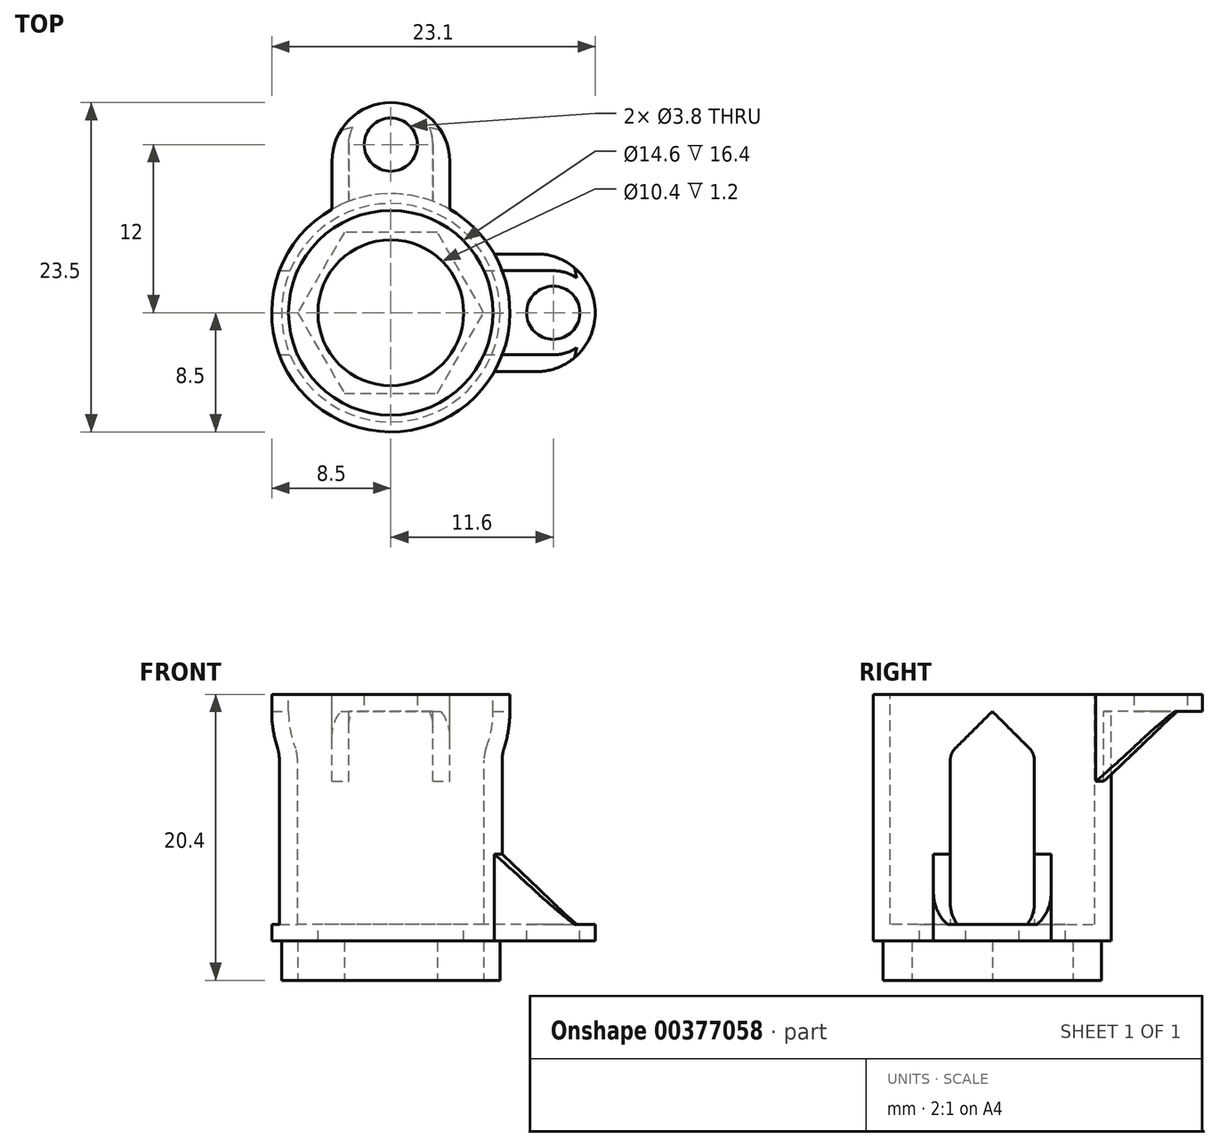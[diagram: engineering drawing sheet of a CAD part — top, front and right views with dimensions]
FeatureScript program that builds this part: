
annotation { "Feature Type Name" : "Feature", "Feature Type Description" : "" }
export const myFeature = defineFeature(function(context is Context, id is Id, definition is map)
    precondition{}
    {
        {
            var Q0;
            Q0=qCreatedBy(makeId("Front.planeOp"),FACE);
            var sketch = newSketch(context, id + "F0", { "sketchPlane" : qUnion([Q0])});
            skLineSegment(sketch, "E0", {"start": v(6.5, 0) * mm, "end": v(6.5, 26.4) * mm});
            skLineSegment(sketch, "E1", {"start": v(4.7, 0) * mm, "end": v(4.7, -6.4) * mm});
            skLineSegment(sketch, "E2", {"start": v(-3.7, 28.3) * mm, "end": v(3.7, 28.3) * mm});
            skPoint(sketch, "E3", {"position": v(0, 28.3) * mm});
            skLineSegment(sketch, "E4", {"start": v(-3.7, 40.8) * mm, "end": v(3.7, 40.8) * mm});
            skLineSegment(sketch, "E5", {"start": v(0, 26.4) * mm, "end": v(0, 0) * mm, "construction": true});
            skSolve(sketch);
        }
        {
            var Q0;
            Q0=qCreatedBy(makeId("Front.planeOp"),FACE);
            var sketch = newSketch(context, id + "F1", { "sketchPlane" : qUnion([Q0])});
            skLineSegment(sketch, "E6", {"start": v(7.3, 0) * mm, "end": v(7.3, 16.4) * mm});
            skLineSegment(sketch, "E7", {"start": v(7.3, 0) * mm, "end": v(5.2, 0) * mm});
            skLineSegment(sketch, "E8", {"start": v(5.2, 0) * mm, "end": v(5.2, -4) * mm});
            skLineSegment(sketch, "E9", {"start": v(5.2, -4) * mm, "end": v(7.8, -4) * mm});
            skLineSegment(sketch, "E10", {"start": v(7.8, -4) * mm, "end": v(7.8, -1.2) * mm});
            skLineSegment(sketch, "E11", {"start": v(8.5, -1.2) * mm, "end": v(8.5, 16.4) * mm});
            skLineSegment(sketch, "E12", {"start": v(7.3, 16.4) * mm, "end": v(8.5, 16.4) * mm});
            skPoint(sketch, "E13.orphan", {"position": v(0, -4) * mm});
            skLineSegment(sketch, "E14", {"start": v(8.5, -1.2) * mm, "end": v(7.8, -1.2) * mm});
            skSolve(sketch);
        }
        {
            var Q0;
            Q0 = qSketchRegion(id + "F1", true);
            var Q1;
            Q1=sQuery(id+"F0.wireOp",EDGE,"E5");
            revolve(context, id + "F2", {"entities" : qUnion([Q0]), "axis" : qUnion([Q1]), "revolveType" : RevolveType.FULL});
        }
        {
            var Q0;
            Q0=makeQuery(id+"F2.opRevolve","SWEPT_FACE",FACE,{"disambiguationData":[OSD([sQuery(id+"F1.wireOp",EDGE,"E9")])]});
            var sketch = newSketch(context, id + "F3", { "sketchPlane" : qUnion([Q0])});
            skCircle(sketch, "E15.cCircle", {"center": v(0, 0) * mm, "radius": 5.75 * mm, "construction": true});
            skLineSegment(sketch, "E15.0", {"start": v(-3.32, 5.75) * mm, "end": v(3.32, 5.75) * mm});
            skLineSegment(sketch, "E15.1", {"start": v(3.32, 5.75) * mm, "end": v(6.64, 0) * mm});
            skLineSegment(sketch, "E15.2", {"start": v(6.64, 0) * mm, "end": v(3.32, -5.75) * mm});
            skLineSegment(sketch, "E15.3", {"start": v(3.32, -5.75) * mm, "end": v(-3.32, -5.75) * mm});
            skLineSegment(sketch, "E15.4", {"start": v(-3.32, -5.75) * mm, "end": v(-6.64, 0) * mm});
            skLineSegment(sketch, "E15.5", {"start": v(-6.64, 0) * mm, "end": v(-3.32, 5.75) * mm});
            skPoint(sketch, "E15.0.midPoint", {"position": v(0, 5.75) * mm});
            skSolve(sketch);
        }
        {
            var Q0;
            Q0 = qSketchRegion(id + "F3", true);
            var Q1;
            Q1=qCreatedBy(makeId("Top.planeOp"),FACE);
            extrude(context, id + "F4", {"entities" : qUnion([Q0]), "operationType" : NewBodyOperationType.REMOVE, "oppositeDirection" : true, "endBoundEntityFace" : qUnion([Q1]), "depth" : (4 - 1.2) * mm});
        }
        {
            var Q0;
            Q0=makeQuery(id+"F2.opRevolve","SWEPT_FACE",FACE,{"disambiguationData":[OSD([sQuery(id+"F1.wireOp",EDGE,"E12")])]});
            var sketch = newSketch(context, id + "F5", { "sketchPlane" : qUnion([Q0])});
            skArc(sketch, "E16", {"start": v(4.2, 7.39) * mm, "mid": v(0, 8.5) * mm, "end": v(-4.2, 7.39) * mm});
            skArc(sketch, "E17", {"start": v(4.2, 10.8) * mm, "mid": v(0, 15) * mm, "end": v(-4.2, 10.8) * mm});
            skPoint(sketch, "E18", {"position": v(0, 15) * mm});
            skLineSegment(sketch, "E19", {"start": v(4.2, 10.8) * mm, "end": v(4.2, 7.39) * mm});
            skLineSegment(sketch, "E20", {"start": v(-4.2, 10.8) * mm, "end": v(-4.2, 7.39) * mm});
            skCircle(sketch, "E21", {"center": v(0, 12) * mm, "radius": 3 * mm, "construction": true});
            skPoint(sketch, "E22", {"position": v(-3, 12) * mm});
            skSolve(sketch);
        }
        {
            var Q0;
            Q0 = qSketchRegion(id + "F5", true);
            var Q1;
            Q1=qCreatedBy(makeId("Top.planeOp"),FACE);
            extrude(context, id + "F6", {"entities" : qUnion([Q0]), "operationType" : NewBodyOperationType.ADD, "endBound" : BoundingType.UP_TO_SURFACE, "oppositeDirection" : true, "endBoundEntityFace" : qUnion([Q1]), "depth" : 9 * mm});
        }
        {
            var Q0;
            Q0=qCreatedBy(makeId("Right.planeOp"),FACE);
            var sketch = newSketch(context, id + "F7", { "sketchPlane" : qUnion([Q0])});
            skLineSegment(sketch, "E23", {"start": v(15, 16.4) * mm, "end": v(15, 15.2) * mm, "construction": true});
            skLineSegment(sketch, "E24", {"start": v(13.5, 15.2) * mm, "end": v(8.5, 10.2) * mm});
            skLineSegment(sketch, "E25", {"start": v(8.5, 10.2) * mm, "end": v(8.5, 16.4) * mm, "construction": true});
            skLineSegment(sketch, "E26", {"start": v(8.5, 10.2) * mm, "end": v(8.5, 0) * mm});
            skLineSegment(sketch, "E27", {"start": v(8.5, 0) * mm, "end": v(15, 0) * mm});
            skLineSegment(sketch, "E28", {"start": v(15, 0) * mm, "end": v(15, 15.2) * mm});
            skLineSegment(sketch, "E29", {"start": v(13.5, 15.2) * mm, "end": v(15, 15.2) * mm});
            skSolve(sketch);
        }
        {
            var Q0;
            Q0 = qSketchRegion(id + "F7", true);
            var Q1;
            Q1=sQuery(id+"F0.wireOp",EDGE,"E5");
            revolve(context, id + "F8", {"operationType" : NewBodyOperationType.REMOVE, "entities" : qUnion([Q0]), "axis" : qUnion([Q1]), "revolveType" : RevolveType.FULL, "oppositeDirection" : true});
        }
        {
            var Q0;
            Q0=makeQuery(id+"F5.imprint","IMPRINT",FACE,{"disambiguationData":[TD([[makeQuery(id+"F5.imprint","IMPRINT",EDGE,{"derivedFrom":sQuery(id+"F5.wireOp",EDGE,"E16")}),-1.0]])]});
            cPlane(context, id + "F9", {"entities" : qUnion([Q0]), "cplaneType" : CPlaneType.OFFSET, "offset" : 1.2 * mm, "oppositeDirection" : true, "width" : 150 * mm, "height" : 150 * mm});
        }
        {
            var Q0;
            Q0=qCreatedBy(id+"F9.planeOp",FACE);
            var sketch = newSketch(context, id + "F10", { "sketchPlane" : qUnion([Q0])});
            skArc(sketch, "E30", {"start": v(3, 12) * mm, "mid": v(0, 15) * mm, "end": v(-3, 12) * mm});
            skArc(sketch, "E31", {"start": v(3, 7.95) * mm, "mid": v(0, 8.5) * mm, "end": v(-3, 7.95) * mm});
            skLineSegment(sketch, "E32", {"start": v(-3, 12) * mm, "end": v(-3, 7.95) * mm});
            skLineSegment(sketch, "E33", {"start": v(3, 12) * mm, "end": v(3, 7.95) * mm});
            skPoint(sketch, "E34", {"position": v(0, 15) * mm});
            skSolve(sketch);
        }
        {
            var Q0;
            Q0 = qSketchRegion(id + "F10", true);
            extrude(context, id + "F11", {"entities" : qUnion([Q0]), "operationType" : NewBodyOperationType.REMOVE, "endBound" : BoundingType.UP_TO_NEXT, "oppositeDirection" : true, "depth" : 25 * mm});
        }
        {
            var Q0;
            Q0=qCreatedBy(id+"F9.planeOp",FACE);
            var sketch = newSketch(context, id + "F12", { "sketchPlane" : qUnion([Q0])});
            skCircle(sketch, "E35", {"center": v(0, 12) * mm, "radius": 1.9 * mm});
            skSolve(sketch);
        }
        {
            var Q0;
            Q0 = qSketchRegion(id + "F12", true);
            extrude(context, id + "F13", {"entities" : qUnion([Q0]), "operationType" : NewBodyOperationType.REMOVE, "endBound" : BoundingType.UP_TO_NEXT, "depth" : 25 * mm});
        }
        {
            var Q0;
            Q0=qCreatedBy(makeId("Top.planeOp"),FACE);
            var sketch = newSketch(context, id + "F14", { "sketchPlane" : qUnion([Q0])});
            skArc(sketch, "E36", {"start": v(7.39, -4.2) * mm, "mid": v(8.5, 0) * mm, "end": v(7.39, 4.2) * mm});
            skCircle(sketch, "E37", {"center": v(11.6, 0) * mm, "radius": 3 * mm, "construction": true});
            skArc(sketch, "E38", {"start": v(10.4, -4.2) * mm, "mid": v(14.6, 0) * mm, "end": v(10.4, 4.2) * mm});
            skPoint(sketch, "E39", {"position": v(14.6, 0) * mm});
            skPoint(sketch, "E40", {"position": v(10.4, 4.2) * mm});
            skPoint(sketch, "E41", {"position": v(11.6, 3) * mm});
            skLineSegment(sketch, "E42", {"start": v(10.4, 4.2) * mm, "end": v(7.39, 4.2) * mm});
            skLineSegment(sketch, "E43", {"start": v(10.4, -4.2) * mm, "end": v(7.39, -4.2) * mm});
            skSolve(sketch);
        }
        {
            var Q0;
            Q0 = qSketchRegion(id + "F14", true);
            extrude(context, id + "F15", {"entities" : qUnion([Q0]), "operationType" : NewBodyOperationType.ADD, "depth" : 5 * mm, "hasSecondDirection" : true, "secondDirectionOppositeDirection" : true, "secondDirectionDepth" : 1.2 * mm});
        }
        {
            var Q0;
            Q0=qCreatedBy(makeId("Front.planeOp"),FACE);
            var sketch = newSketch(context, id + "F16", { "sketchPlane" : qUnion([Q0])});
            skLineSegment(sketch, "E44", {"start": v(8.5, 5) * mm, "end": v(14.6, 5) * mm});
            skLineSegment(sketch, "E45", {"start": v(13.5, 0) * mm, "end": v(8.5, 5) * mm});
            skLineSegment(sketch, "E46", {"start": v(13.5, 0) * mm, "end": v(14.6, 0) * mm});
            skLineSegment(sketch, "E47", {"start": v(14.6, 0) * mm, "end": v(14.6, 5) * mm});
            skSolve(sketch);
        }
        {
            var Q0;
            Q0 = qSketchRegion(id + "F16", true);
            var Q1;
            Q1=sQuery(id+"F0.wireOp",EDGE,"E5");
            revolve(context, id + "F17", {"operationType" : NewBodyOperationType.REMOVE, "entities" : qUnion([Q0]), "axis" : qUnion([Q1]), "revolveType" : RevolveType.FULL, "oppositeDirection" : true});
        }
        {
            var Q0;
            Q0=qCreatedBy(makeId("Top.planeOp"),FACE);
            var sketch = newSketch(context, id + "F18", { "sketchPlane" : qUnion([Q0])});
            skArc(sketch, "E48", {"start": v(7.95, -3) * mm, "mid": v(8.5, 0) * mm, "end": v(7.95, 3) * mm});
            skArc(sketch, "E49", {"start": v(11.6, -3) * mm, "mid": v(14.6, 0) * mm, "end": v(11.6, 3) * mm});
            skLineSegment(sketch, "E50", {"start": v(11.6, 3) * mm, "end": v(7.95, 3) * mm});
            skLineSegment(sketch, "E51", {"start": v(11.6, -3) * mm, "end": v(7.95, -3) * mm});
            skSolve(sketch);
        }
        {
            var Q0;
            Q0 = qSketchRegion(id + "F18", true);
            extrude(context, id + "F19", {"entities" : qUnion([Q0]), "operationType" : NewBodyOperationType.REMOVE, "depth" : 6 * mm});
        }
        {
            var Q0;
            Q0=qCreatedBy(makeId("Top.planeOp"),FACE);
            var sketch = newSketch(context, id + "F20", { "sketchPlane" : qUnion([Q0])});
            skCircle(sketch, "E52", {"center": v(11.6, 0) * mm, "radius": 1.9 * mm});
            skSolve(sketch);
        }
        {
            var Q0;
            Q0 = qSketchRegion(id + "F20", true);
            extrude(context, id + "F21", {"entities" : qUnion([Q0]), "operationType" : NewBodyOperationType.REMOVE, "endBound" : BoundingType.UP_TO_NEXT, "oppositeDirection" : true, "depth" : 25 * mm});
        }
        {
            var Q0;
            Q0=qCreatedBy(makeId("Right.planeOp"),FACE);
            var sketch = newSketch(context, id + "F22", { "sketchPlane" : qUnion([Q0])});
            skLineSegment(sketch, "E53.bottom", {"start": v(-3, 0) * mm, "end": v(3, 0) * mm});
            skLineSegment(sketch, "E53.left", {"start": v(-3, 0) * mm, "end": v(-3, 11.7) * mm});
            skLineSegment(sketch, "E53.right", {"start": v(3, 0) * mm, "end": v(3, 11.7) * mm});
            skLineSegment(sketch, "E54", {"start": v(-2.65, 12.55) * mm, "end": v(0, 15.2) * mm});
            skLineSegment(sketch, "E55", {"start": v(0, 15.2) * mm, "end": v(2.65, 12.55) * mm});
            skPoint(sketch, "E56.visualSharp", {"position": v(-3, 12.2) * mm});
            skArc(sketch, "E56.filletArc", {"start": v(-2.65, 12.55) * mm, "mid": v(-2.9, 12.16) * mm, "end": v(-3, 11.7) * mm});
            skPoint(sketch, "E57.visualSharp", {"position": v(3, 12.2) * mm});
            skArc(sketch, "E57.filletArc", {"start": v(3, 11.7) * mm, "mid": v(2.9, 12.16) * mm, "end": v(2.65, 12.55) * mm});
            skSolve(sketch);
        }
        {
            var Q0;
            Q0 = qSketchRegion(id + "F22", true);
            var Q1;
            Q1=makeQuery(id+"F19.boolean.opBoolean","COPY",VERTEX,{"derivedFrom":makeQuery(id+"F19.opExtrude","CAP_VERTEX",VERTEX,{"disambiguationData":[OSD([sQuery(id+"F18.wireOp",EDGE,"E49"),sQuery(id+"F18.wireOp",EDGE,"E51")])],"isStart":true})});
            extrude(context, id + "F23", {"entities" : qUnion([Q0]), "operationType" : NewBodyOperationType.REMOVE, "endBound" : BoundingType.THROUGH_ALL, "oppositeDirection" : true, "depth" : 25 * mm, "hasSecondDirection" : true, "secondDirectionBound" : SecondDirectionBoundingType.UP_TO_VERTEX, "secondDirectionOppositeDirection" : false, "secondDirectionBoundEntityVertex" : qUnion([Q1]), "secondDirectionDepth" : 25 * mm});
        }
    });
